# Revit family: QF_MACOM_PAX_PL
name_source: partatom
category: Equipamento especial
units: mm (PartAtom-declared; Revit-internal decimal feet)

## family parameters
Com base no plano de trabalho = Não
Compartilhado = Não
Corte com vazios quando carregada = Não
Cota do conector redondo = Utilizar diâmetro
Número OmniClass = 23.40.40.14.24.14
Ponto de cálculo do ambiente = Não
Sempre na vertical = Sim
Tipo de parte = Normal
Título OmniClass = Service Line Equipment

## types (5) — shared parameters
Cycle = 60 Hz
Descrição = PISTA AQUECIDA PLANA INOX PLUG-IN MACOM
Electric Connection Height = 229,000 mm
Elevação padrão = 0,000 mm
Fabricante = MACOM
Height = 370,000 mm
URL = https://www.acosmacom.com.br
Volts = 220 V
Weight = 0 kg
Width = 590,000 mm
Work Temperature = 20°C a 95°C

## per-type parameters (varying)
| type | Electric Power | GN Capacity 1/1 | Length | Volume |
| PA2-PL | 2000 W | 02 | 715,000 mm | 0,15 m³ |
| PA3-PL | 3000 W | 03 | 1040,000 mm | 0,22 m³ |
| PA4-PL | 4000 W | 04 | 1365,000 mm | 0,29 m³ |
| PA5-PL | 5000 W | 05 | 1690,000 mm | 0,36 m³ |
| PA6-PL | 6000 W | 06 | 2015,000 mm | 0,43 m³ |

note: column(s) folded — value = type name in every type: Modelo

## geometry (parser evidence)
native form markers: Sweep x7
no freeform markers — native parametric forms only
